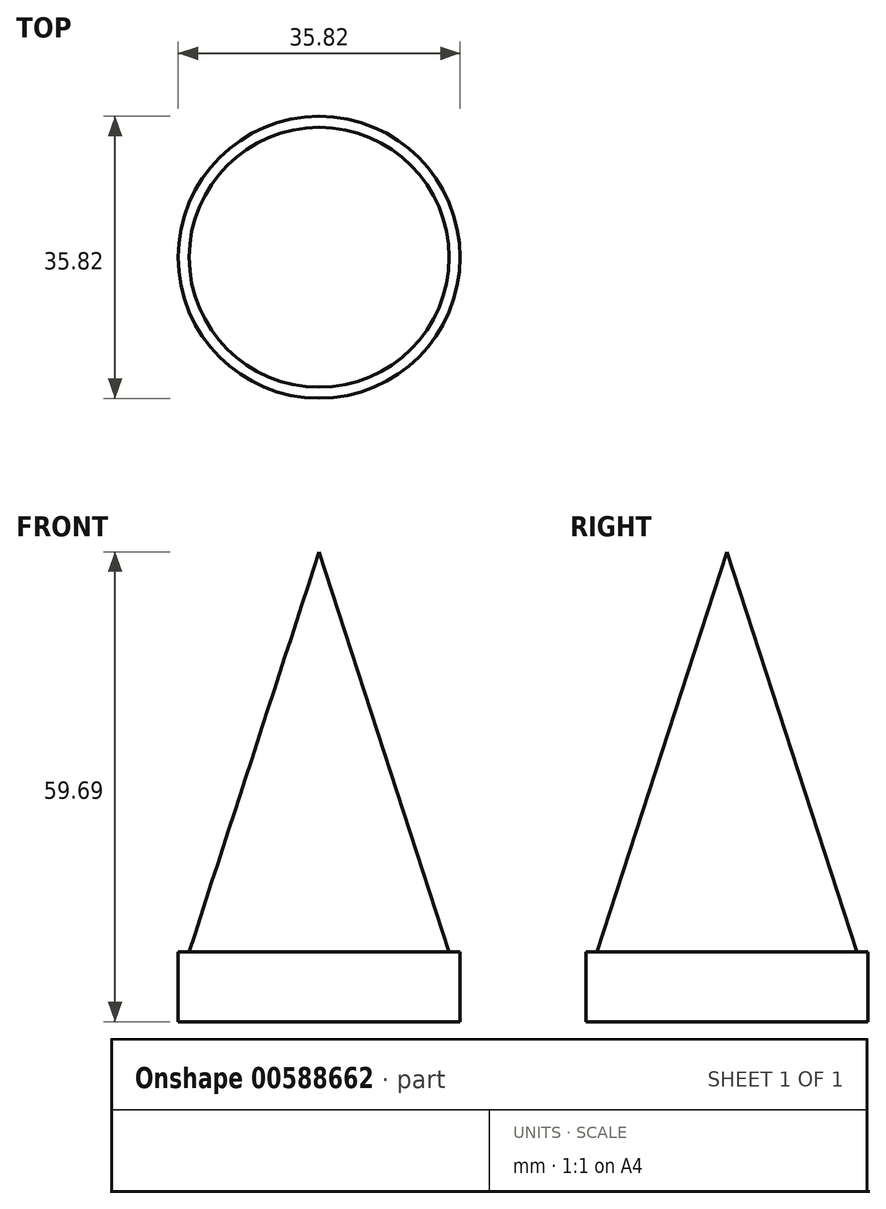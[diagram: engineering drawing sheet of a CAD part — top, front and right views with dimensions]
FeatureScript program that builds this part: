
annotation { "Feature Type Name" : "Feature", "Feature Type Description" : "" }
export const myFeature = defineFeature(function(context is Context, id is Id, definition is map)
    precondition{}
    {
        {
            var Q0;
            Q0=qCreatedBy(makeId("Right.planeOp"),FACE);
            var sketch = newSketch(context, id + "F0", { "sketchPlane" : qUnion([Q0])});
            skPoint(sketch, "E0", {"position": v(-16.51, 0) * mm});
            skPoint(sketch, "E1", {"position": v(0, 0) * mm});
            skPoint(sketch, "E2", {"position": v(0, 50.8) * mm});
            skLineSegment(sketch, "E3", {"start": v(0, 50.8) * mm, "end": v(0, 0) * mm});
            skLineSegment(sketch, "E4", {"start": v(0, 0) * mm, "end": v(-16.51, 0) * mm});
            skLineSegment(sketch, "E5", {"start": v(0, 50.8) * mm, "end": v(-16.51, 0) * mm});
            skPoint(sketch, "E6", {"position": v(0, -8.9) * mm});
            skPoint(sketch, "E7", {"position": v(-17.9, -8.9) * mm});
            skLineSegment(sketch, "E8", {"start": v(-17.9, -8.9) * mm, "end": v(0, -8.9) * mm});
            skLineSegment(sketch, "E9", {"start": v(0, -8.9) * mm, "end": v(0, 0) * mm});
            skPoint(sketch, "E10", {"position": v(-17.9, 0) * mm});
            skLineSegment(sketch, "E11", {"start": v(-16.51, 0) * mm, "end": v(-17.9, 0) * mm});
            skLineSegment(sketch, "E12", {"start": v(-17.9, 0) * mm, "end": v(-17.9, -8.9) * mm});
            skSolve(sketch);
        }
        {
            var Q0;
            Q0=makeQuery(id+"F0.imprint","IMPRINT",FACE,{"disambiguationData":[TD([[makeQuery(id+"F0.imprint","IMPRINT",EDGE,{"derivedFrom":sQuery(id+"F0.wireOp",EDGE,"E3")}),-1.0]])]});
            var Q1;
            Q1=makeQuery(id+"F0.imprint","IMPRINT",FACE,{"disambiguationData":[TD([[makeQuery(id+"F0.imprint","IMPRINT",EDGE,{"derivedFrom":sQuery(id+"F0.wireOp",EDGE,"E4")}),1.0]])]});
            var Q2;
            Q2=sQuery(id+"F0.wireOp",EDGE,"E3");
            revolve(context, id + "F1", {"entities" : qUnion([Q0, Q1]), "axis" : qUnion([Q2]), "revolveType" : RevolveType.FULL});
        }
    });
